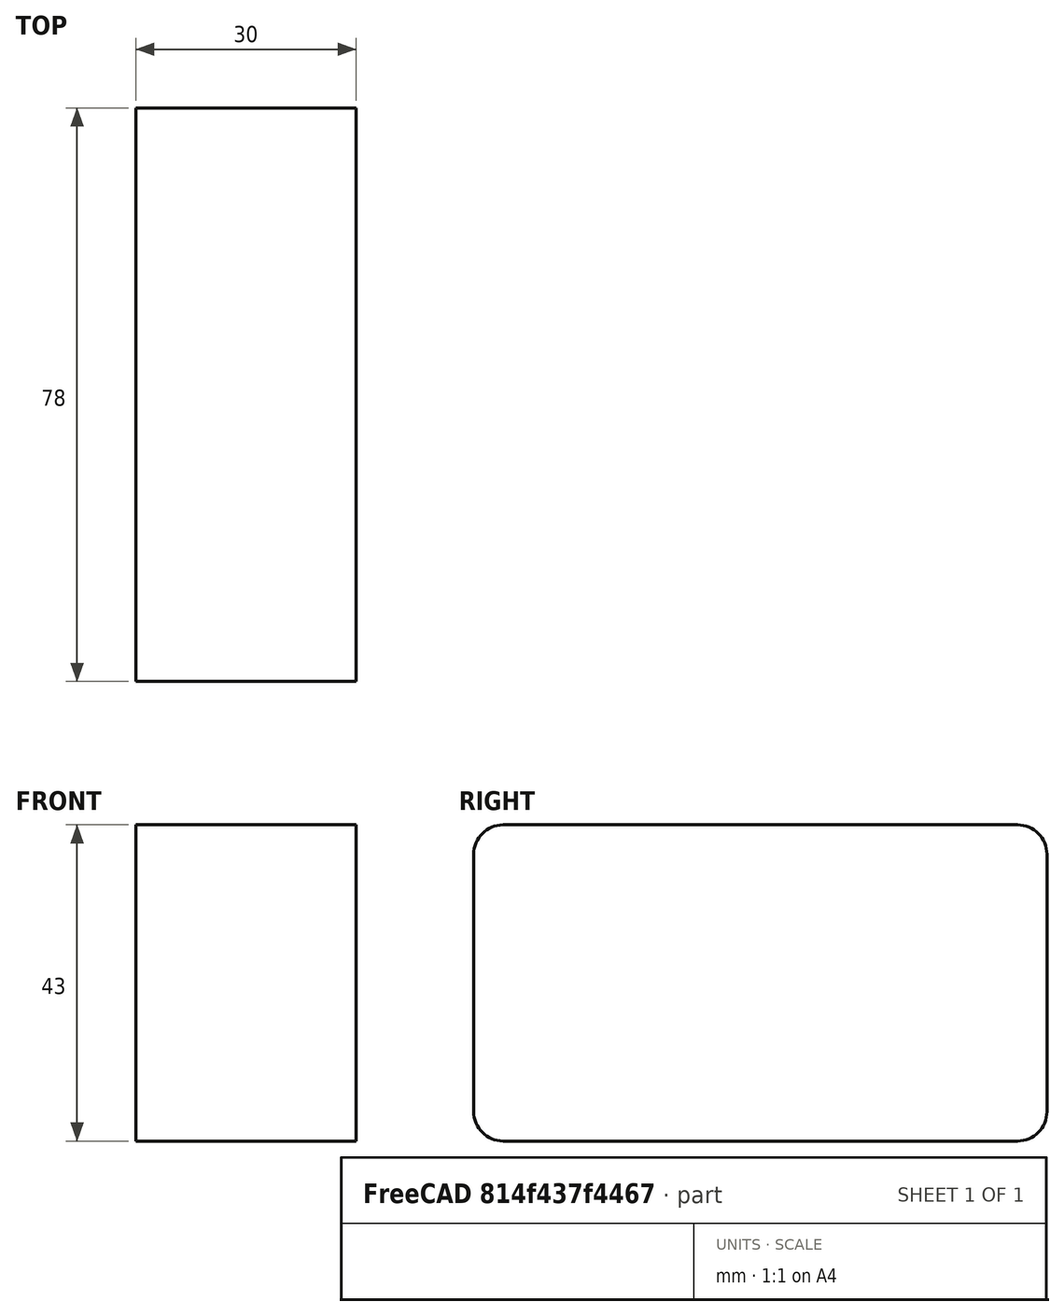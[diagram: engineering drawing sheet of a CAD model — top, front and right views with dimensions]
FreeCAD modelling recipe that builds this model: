
FCSTD DOCUMENT  (FreeCAD 0.19R24267 +148 (Git))
Label: LiulinBoxHammond
License: All rights reserved
LicenseURL: http://en.wikipedia.org/wiki/All_rights_reserved
objects: Sketcher::SketchObject×1, PartDesign::Pad×1, PartDesign::Body×1, App::Part×1
note: 4 computed .brp shape members not serialized (recipe doc carries the construction recipe); baked Part::Feature solids carry a one-line shape summary decoded from their .brp

FEATURE [Sketcher::SketchObject] Sketch
  FullyConstrained = true
  MapMode = 5
  Placement = pos=(0,0,0) rot=(0.57735,0.57735,0.57735;2.0944rad)
  Support = -> [YZ_Plane001]
  sketch-geometry (8):
    g0: LineSegment StartX=-35 StartY=21.5 StartZ=0 EndX=35 EndY=21.5 EndZ=0
    g1: LineSegment StartX=39 StartY=17.5 StartZ=0 EndX=39 EndY=-17.5 EndZ=0
    g2: LineSegment StartX=35 StartY=-21.5 StartZ=0 EndX=-35 EndY=-21.5 EndZ=0
    g3: LineSegment StartX=-39 StartY=-17.5 StartZ=0 EndX=-39 EndY=17.5 EndZ=0
    g4: ArcOfCircle CenterX=35 CenterY=17.5 CenterZ=0 NormalX=0 NormalY=0 NormalZ=1 AngleXU=0 Radius=4 StartAngle=0 EndAngle=1.5708
    g5: ArcOfCircle CenterX=35 CenterY=-17.5 CenterZ=0 NormalX=0 NormalY=0 NormalZ=1 AngleXU=0 Radius=4 StartAngle=4.71239 EndAngle=6.28319
    g6: ArcOfCircle CenterX=-35 CenterY=17.5 CenterZ=0 NormalX=0 NormalY=0 NormalZ=1 AngleXU=0 Radius=4 StartAngle=1.5708 EndAngle=3.14159
    g7: ArcOfCircle CenterX=-35 CenterY=-17.5 CenterZ=0 NormalX=0 NormalY=0 NormalZ=1 AngleXU=0 Radius=4 StartAngle=3.14159 EndAngle=4.71239
  constraints (19):
    c: Horizontal(g0)
    c: Horizontal(g2)
    c: Vertical(g1)
    c: Vertical(g3)
    c: Tangent(g0,g4) = 1.5708
    c: Tangent(g1,g4) = 1.5708
    c: Tangent(g1,g5) = 1.5708
    c: Tangent(g2,g5) = 1.5708
    c: Tangent(g0,g6) = 1.5708
    c: Tangent(g3,g6) = 1.5708
    c: Tangent(g3,g7) = 1.5708
    c: Tangent(g2,g7) = 1.5708
    c: Symmetric(g6,g5,g-1)
    c: Equal(g6,g4)
    c: Equal(g4,g5)
    c: Equal(g5,g7)
    c: DistanceX(g3,g1) = 78  'BlockWidth'
    c: DistanceY(g2,g0) = 43
    c: DistanceX(g5,g1) = 4
FEATURE [PartDesign::Pad] Pad
  Direction = (1,1,1)
  Length = 30
  Length2 = 100
  Placement = pos=(0,0,0) rot=(0.57735,0.57735,0.57735;2.0944rad)
  Profile = -> Sketch
  Type = 0
FEATURE [PartDesign::Body] Body  label="BoxBlock"
  Group = -> [Sketch,Pad]
  Origin = -> Origin001
  Tip = -> Pad
FEATURE [App::Part] Part
  Group = -> [Body]
  Origin = -> Origin
